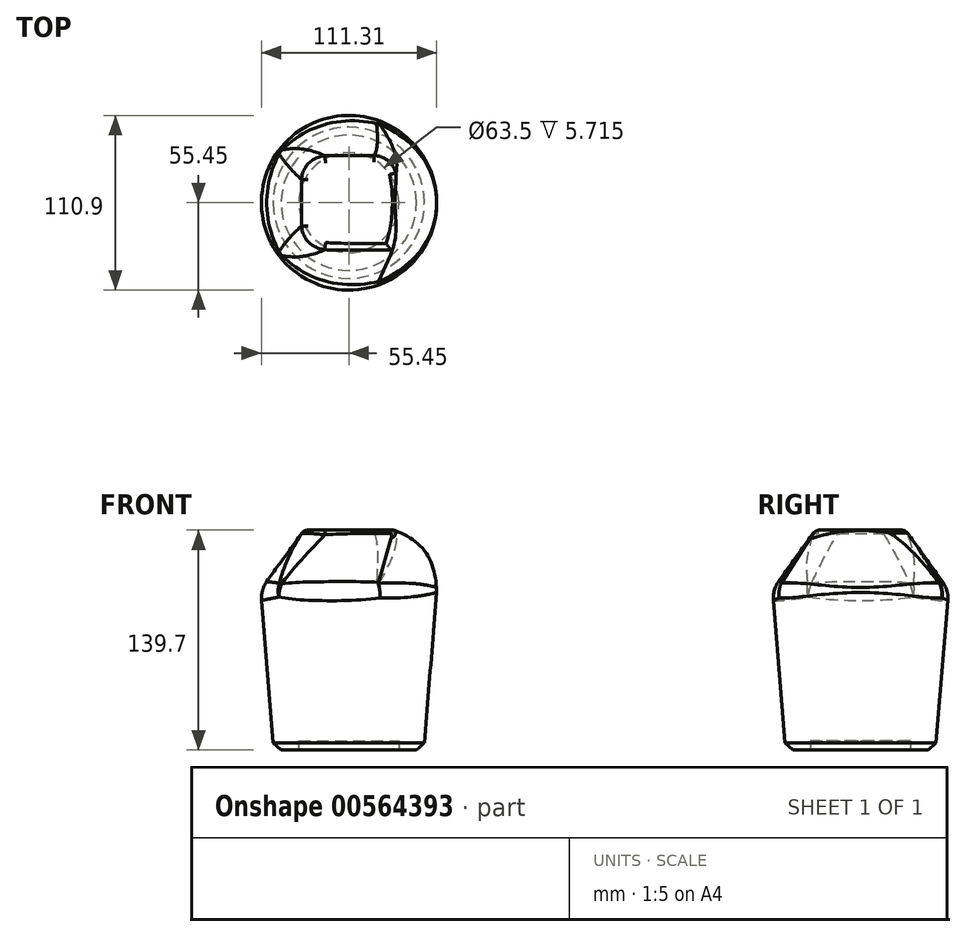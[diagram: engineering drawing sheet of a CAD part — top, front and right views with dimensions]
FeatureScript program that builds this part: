
annotation { "Feature Type Name" : "Feature", "Feature Type Description" : "" }
export const myFeature = defineFeature(function(context is Context, id is Id, definition is map)
    precondition{}
    {
        {
            var Q0;
            Q0=qCreatedBy(makeId("Front.planeOp"),FACE);
            var sketch = newSketch(context, id + "F0", { "sketchPlane" : qUnion([Q0])});
            skLineSegment(sketch, "E0", {"start": v(0, 0) * mm, "end": v(47.63, 0) * mm});
            skLineSegment(sketch, "E1", {"start": v(47.63, 0) * mm, "end": v(55.93, 101.6) * mm});
            skLineSegment(sketch, "E2", {"start": v(55.93, 101.6) * mm, "end": v(0, 101.6) * mm});
            skLineSegment(sketch, "E3", {"start": v(0, 101.6) * mm, "end": v(0, 0) * mm});
            skLineSegment(sketch, "E4", {"start": v(0, 0) * mm, "end": v(0, 82.31) * mm, "construction": true});
            skSolve(sketch);
        }
        {
            var Q0;
            Q0=makeQuery(id+"F0.imprint","IMPRINT",FACE,{"disambiguationData":[TD([[makeQuery(id+"F0.imprint","IMPRINT",EDGE,{"derivedFrom":sQuery(id+"F0.wireOp",EDGE,"E0")}),1.0]])]});
            var Q1;
            Q1=sQuery(id+"F0.wireOp",EDGE,"E3");
            revolve(context, id + "F1", {"entities" : qUnion([Q0]), "axis" : qUnion([Q1]), "revolveType" : RevolveType.FULL});
        }
        {
            var Q0;
            Q0=makeQuery(id+"F1.opRevolve","SWEPT_FACE",FACE,{"disambiguationData":[OSD([sQuery(id+"F0.wireOp",EDGE,"E2")])]});
            cPlane(context, id + "F2", {"entities" : qUnion([Q0]), "cplaneType" : CPlaneType.OFFSET, "offset" : 38.1 * mm, "width" : 152.4 * mm, "height" : 152.4 * mm});
        }
        {
            var Q0;
            Q0=qCreatedBy(id+"F2.planeOp",FACE);
            var sketch = newSketch(context, id + "F3", { "sketchPlane" : qUnion([Q0])});
            skLineSegment(sketch, "E5.bottom", {"start": v(-28.57, -28.58) * mm, "end": v(28.58, -28.58) * mm});
            skLineSegment(sketch, "E5.top", {"start": v(-28.58, 28.58) * mm, "end": v(28.57, 28.58) * mm});
            skLineSegment(sketch, "E5.left", {"start": v(-28.57, -28.58) * mm, "end": v(-28.58, 28.58) * mm});
            skLineSegment(sketch, "E5.right", {"start": v(28.58, -28.58) * mm, "end": v(28.57, 28.58) * mm});
            skPoint(sketch, "E5.middle", {"position": v(0, 0) * mm});
            skSolve(sketch);
        }
        {
            var Q0;
            Q0=qCreatedBy(makeId("Front.planeOp"),FACE);
            var sketch = newSketch(context, id + "F4", { "sketchPlane" : qUnion([Q0])});
            skFitSpline(sketch, "E6", {"points": [v(55.93, 101.6) * mm, v(28.58, 139.7) * mm], "startDerivative": vector(-4.8, 59.46) * mm, "endDerivative": vector(-58.03, 21.3) * mm});
            skSolve(sketch);
        }
        {
            var Q1;
            Q1=makeQuery(id+"F1.opRevolve","SWEPT_FACE",FACE,{"disambiguationData":[OSD([sQuery(id+"F0.wireOp",EDGE,"E2")])]});
            var Q2;
            Q2=makeQuery(id+"F3.imprint","IMPRINT",FACE,{"disambiguationData":[TD([[makeQuery(id+"F3.imprint","IMPRINT",EDGE,{"derivedFrom":sQuery(id+"F3.wireOp",EDGE,"E5.bottom")}),1.0]])]});
            var Q3;
            Q3=sQuery(id+"F4.wireOp",EDGE,"E6");
            loft(context, id + "F5", {"operationType" : NewBodyOperationType.ADD, "addGuides" : true, "sheetProfilesArray" : [{ "sheetProfileEntities" : qUnion([Q1]) }, { "sheetProfileEntities" : qUnion([Q2]) }], "guidesArray" : [{ "guideEntities" : qUnion([Q3]), "guideDerivativeType" : LoftGuideDerivativeType.DEFAULT, "guideDerivativeMagnitude" : 1 }]});
        }
        {
            var Q0;
            Q0=makeQuery(id+"F5.opLoft","MID_CAP_EDGE",EDGE,{"disambiguationData":[OSD([sQuery(id+"F3.wireOp",EDGE,"E5.bottom"),sQuery(id+"F3.wireOp",EDGE,"E5.left"),sQuery(id+"F3.wireOp",EDGE,"E5.right")])],"capPos":1.0});
            var Q1;
            Q1=makeQuery(id+"F5.opLoft","MID_CAP_EDGE",EDGE,{"disambiguationData":[OSD([sQuery(id+"F3.wireOp",EDGE,"E5.bottom"),sQuery(id+"F3.wireOp",EDGE,"E5.top"),sQuery(id+"F3.wireOp",EDGE,"E5.left")])],"capPos":1.0});
            var Q2;
            Q2=makeQuery(id+"F5.opLoft","MID_CAP_EDGE",EDGE,{"disambiguationData":[OSD([sQuery(id+"F3.wireOp",EDGE,"E5.top"),sQuery(id+"F3.wireOp",EDGE,"E5.left"),sQuery(id+"F3.wireOp",EDGE,"E5.right")])],"capPos":1.0});
            var Q3;
            Q3=makeQuery(id+"F5.opLoft","MID_CAP_EDGE",EDGE,{"disambiguationData":[OSD([sQuery(id+"F3.wireOp",EDGE,"E5.bottom"),sQuery(id+"F3.wireOp",EDGE,"E5.right"),sQuery(id+"F4.wireOp",EDGE,"E6")])],"capPos":1.0});
            fillet(context, id + "F6", {"entities" : qUnion([Q0, Q1, Q2, Q3]), "radius" : 5.08 * mm, "tangentPropagation" : true, "allowEdgeOverflow" : false});
        }
        {
            var Q0;
            Q0=makeQuery(id+"F5.opLoft","SWEPT_EDGE",EDGE,{"disambiguationData":[OSD([sQuery(id+"F0.wireOp",EDGE,"E1"),sQuery(id+"F0.wireOp",EDGE,"E2"),sQuery(id+"F3.wireOp",EDGE,"E5.bottom"),sQuery(id+"F3.wireOp",EDGE,"E5.top"),sQuery(id+"F3.wireOp",EDGE,"E5.left")])]});
            var Q1;
            Q1=makeQuery(id+"F5.opLoft","SWEPT_EDGE",EDGE,{"disambiguationData":[OSD([sQuery(id+"F0.wireOp",EDGE,"E1"),sQuery(id+"F0.wireOp",EDGE,"E2"),sQuery(id+"F3.wireOp",EDGE,"E5.bottom"),sQuery(id+"F3.wireOp",EDGE,"E5.left"),sQuery(id+"F3.wireOp",EDGE,"E5.right")])]});
            var Q2;
            Q2=makeQuery(id+"F5.opLoft","SWEPT_EDGE",EDGE,{"disambiguationData":[OSD([sQuery(id+"F0.wireOp",EDGE,"E1"),sQuery(id+"F0.wireOp",EDGE,"E2"),sQuery(id+"F3.wireOp",EDGE,"E5.top"),sQuery(id+"F3.wireOp",EDGE,"E5.right"),sQuery(id+"F4.wireOp",EDGE,"E6")])]});
            var Q3;
            Q3=makeQuery(id+"F5.opLoft","SWEPT_EDGE",EDGE,{"disambiguationData":[OSD([sQuery(id+"F0.wireOp",EDGE,"E1"),sQuery(id+"F0.wireOp",EDGE,"E2"),sQuery(id+"F3.wireOp",EDGE,"E5.top"),sQuery(id+"F3.wireOp",EDGE,"E5.left"),sQuery(id+"F3.wireOp",EDGE,"E5.right")])]});
            fillet(context, id + "F7", {"entities" : qUnion([Q0, Q1, Q2, Q3]), "radius" : 17.78 * mm, "tangentPropagation" : true, "allowEdgeOverflow" : false});
        }
        {
            var Q0;
            Q0=makeQuery(id+"F1.opRevolve","SWEPT_EDGE",EDGE,{"disambiguationData":[OSD([sQuery(id+"F0.wireOp",EDGE,"E1"),sQuery(id+"F0.wireOp",EDGE,"E2")])]});
            fillet(context, id + "F8", {"entities" : qUnion([Q0]), "radius" : 17.78 * mm, "tangentPropagation" : true, "allowEdgeOverflow" : false});
        }
        {
            var Q0;
            Q0=makeQuery(id+"F1.opRevolve","SWEPT_FACE",FACE,{"disambiguationData":[OSD([sQuery(id+"F0.wireOp",EDGE,"E0")])]});
            var sketch = newSketch(context, id + "F9", { "sketchPlane" : qUnion([Q0])});
            skCircle(sketch, "E7", {"center": v(0, 0) * mm, "radius": 31.75 * mm});
            skSolve(sketch);
        }
        {
            var Q0;
            Q0=makeQuery(id+"F9.imprint","IMPRINT",FACE,{"disambiguationData":[TD([[makeQuery(id+"F9.imprint","IMPRINT",EDGE,{"derivedFrom":sQuery(id+"F9.wireOp",EDGE,"E7")}),1.0]])]});
            extrude(context, id + "F10", {"entities" : qUnion([Q0]), "operationType" : NewBodyOperationType.REMOVE, "oppositeDirection" : true, "depth" : 5.7 * mm, "offsetDistance" : 25.4 * mm});
        }
        {
            var Q0;
            Q0=makeQuery(id+"F1.opRevolve","SWEPT_EDGE",EDGE,{"disambiguationData":[OSD([sQuery(id+"F0.wireOp",EDGE,"E0"),sQuery(id+"F0.wireOp",EDGE,"E1")])]});
            var Q1;
            Q1=makeQuery(id+"F10.boolean.opBoolean","COPY",EDGE,{"derivedFrom":makeQuery(id+"F10.opExtrude","CAP_EDGE",EDGE,{"disambiguationData":[OSD([sQuery(id+"F9.wireOp",EDGE,"E7")])],"isStart":true})});
            chamfer(context, id + "F11", {"entities" : qUnion([Q0, Q1]), "width" : 5.08 * mm, "tangentPropagation" : true});
        }
    });
